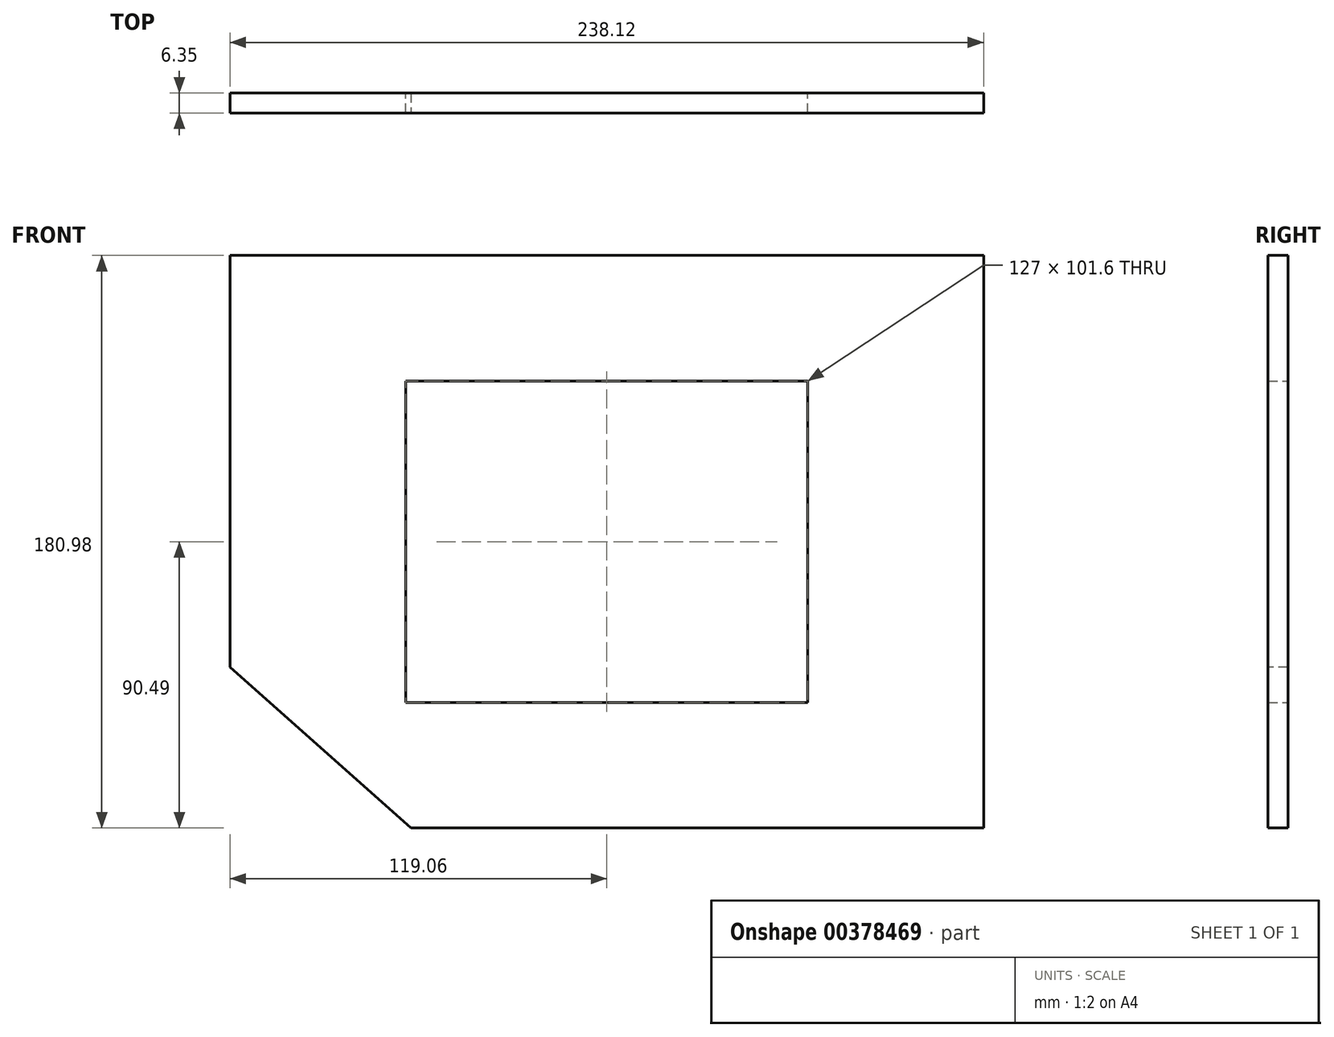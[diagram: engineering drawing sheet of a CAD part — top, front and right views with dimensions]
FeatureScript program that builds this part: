
annotation { "Feature Type Name" : "Feature", "Feature Type Description" : "" }
export const myFeature = defineFeature(function(context is Context, id is Id, definition is map)
    precondition{}
    {
        {
            var Q0;
            Q0=qCreatedBy(makeId("Front.planeOp"),FACE);
            var sketch = newSketch(context, id + "F0", { "sketchPlane" : qUnion([Q0])});
            skLineSegment(sketch, "E0.bottom", {"start": v(119.06, 90.49) * mm, "end": v(-119.06, 90.49) * mm});
            skLineSegment(sketch, "E0.top", {"start": v(96.01, -90.49) * mm, "end": v(-88.14, -90.49) * mm});
            skLineSegment(sketch, "E0.left", {"start": v(119.06, 90.49) * mm, "end": v(119.06, -65) * mm});
            skLineSegment(sketch, "E0.right", {"start": v(-119.06, 90.49) * mm, "end": v(-119.06, -59.1) * mm});
            skPoint(sketch, "E0.middle", {"position": v(0, 0) * mm});
            skPoint(sketch, "E1.orphan", {"position": v(-119.06, -90.49) * mm});
            skPoint(sketch, "E2.orphan", {"position": v(119.06, -90.49) * mm});
            skLineSegment(sketch, "E3", {"start": v(-119.06, -59.1) * mm, "end": v(-119.06, -90.49) * mm});
            skLineSegment(sketch, "E4", {"start": v(-88.14, -90.49) * mm, "end": v(-119.06, -90.49) * mm});
            skLineSegment(sketch, "E5", {"start": v(96.01, -90.49) * mm, "end": v(119.06, -90.49) * mm});
            skLineSegment(sketch, "E6", {"start": v(119.06, -65) * mm, "end": v(119.06, -90.49) * mm});
            skLineSegment(sketch, "E7.bottom", {"start": v(63.5, 50.8) * mm, "end": v(-63.5, 50.8) * mm});
            skLineSegment(sketch, "E7.top", {"start": v(63.5, -50.8) * mm, "end": v(-63.5, -50.8) * mm});
            skLineSegment(sketch, "E7.left", {"start": v(63.5, 50.8) * mm, "end": v(63.5, -50.8) * mm});
            skLineSegment(sketch, "E7.right", {"start": v(-63.5, 50.8) * mm, "end": v(-63.5, -50.8) * mm});
            skSolve(sketch);
        }
        {
            var Q0;
            Q0 = qSketchRegion(id + "F0", true);
            extrude(context, id + "F1", {"entities" : qUnion([Q0]), "depth" : 6.35 * mm});
        }
        {
            var Q0;
            Q0=makeQuery(id+"F1.opExtrude","CAP_FACE",FACE,{"disambiguationData":[OSD([sQuery(id+"F0.wireOp",EDGE,"E0.bottom"),sQuery(id+"F0.wireOp",EDGE,"E0.top"),sQuery(id+"F0.wireOp",EDGE,"E0.left"),sQuery(id+"F0.wireOp",EDGE,"E0.right"),sQuery(id+"F0.wireOp",EDGE,"E3"),sQuery(id+"F0.wireOp",EDGE,"E4"),sQuery(id+"F0.wireOp",EDGE,"E5"),sQuery(id+"F0.wireOp",EDGE,"E6")])],"isStart":false});
            var sketch = newSketch(context, id + "F2", { "sketchPlane" : qUnion([Q0])});
            skLineSegment(sketch, "E8", {"start": v(61.91, -90.49) * mm, "end": v(119.06, -90.49) * mm});
            skLineSegment(sketch, "E9", {"start": v(119.06, -90.49) * mm, "end": v(119.06, -39.69) * mm});
            skPoint(sketch, "E10.start.orphan", {"position": v(-119.06, -39.69) * mm});
            skPoint(sketch, "E11.end.orphan", {"position": v(-61.91, -90.49) * mm});
            skLineSegment(sketch, "E12", {"start": v(-119.06, -90.49) * mm, "end": v(-119.06, -39.69) * mm});
            skLineSegment(sketch, "E13", {"start": v(-61.91, -90.49) * mm, "end": v(-119.06, -39.69) * mm});
            skLineSegment(sketch, "E14", {"start": v(-61.91, -90.49) * mm, "end": v(-119.06, -90.49) * mm});
            skSolve(sketch);
        }
        {
            var Q0;
            Q0 = qSketchRegion(id + "F2", true);
            extrude(context, id + "F3", {"entities" : qUnion([Q0]), "operationType" : NewBodyOperationType.REMOVE, "oppositeDirection" : true, "depth" : 25.4 * mm});
        }
    });
